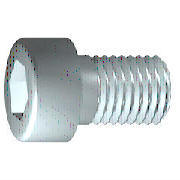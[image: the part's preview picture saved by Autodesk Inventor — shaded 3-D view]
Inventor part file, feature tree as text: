
AUTODESK INVENTOR PART (.ipt)
format: ipt  version: 2024 (Build 280153000, 153)  size: 187,904 bytes
history: native  units: mm (DEFAULTED — no unit token found)
features: extrude x1, plane x1, fillet x1
ambient origin geometry x7: Origin, YZ Plane, XY Plane, X Axis, Y Axis, Z Axis, Center Point
bodies: Solid1 (feature_tree), Body (feature_tree)
feature tree (3):
  extrude  "Slot"  Depth=12.0mm
  plane  "Work Plane1"
  fillet  "Fillet2"  Radius=0.306825mm
